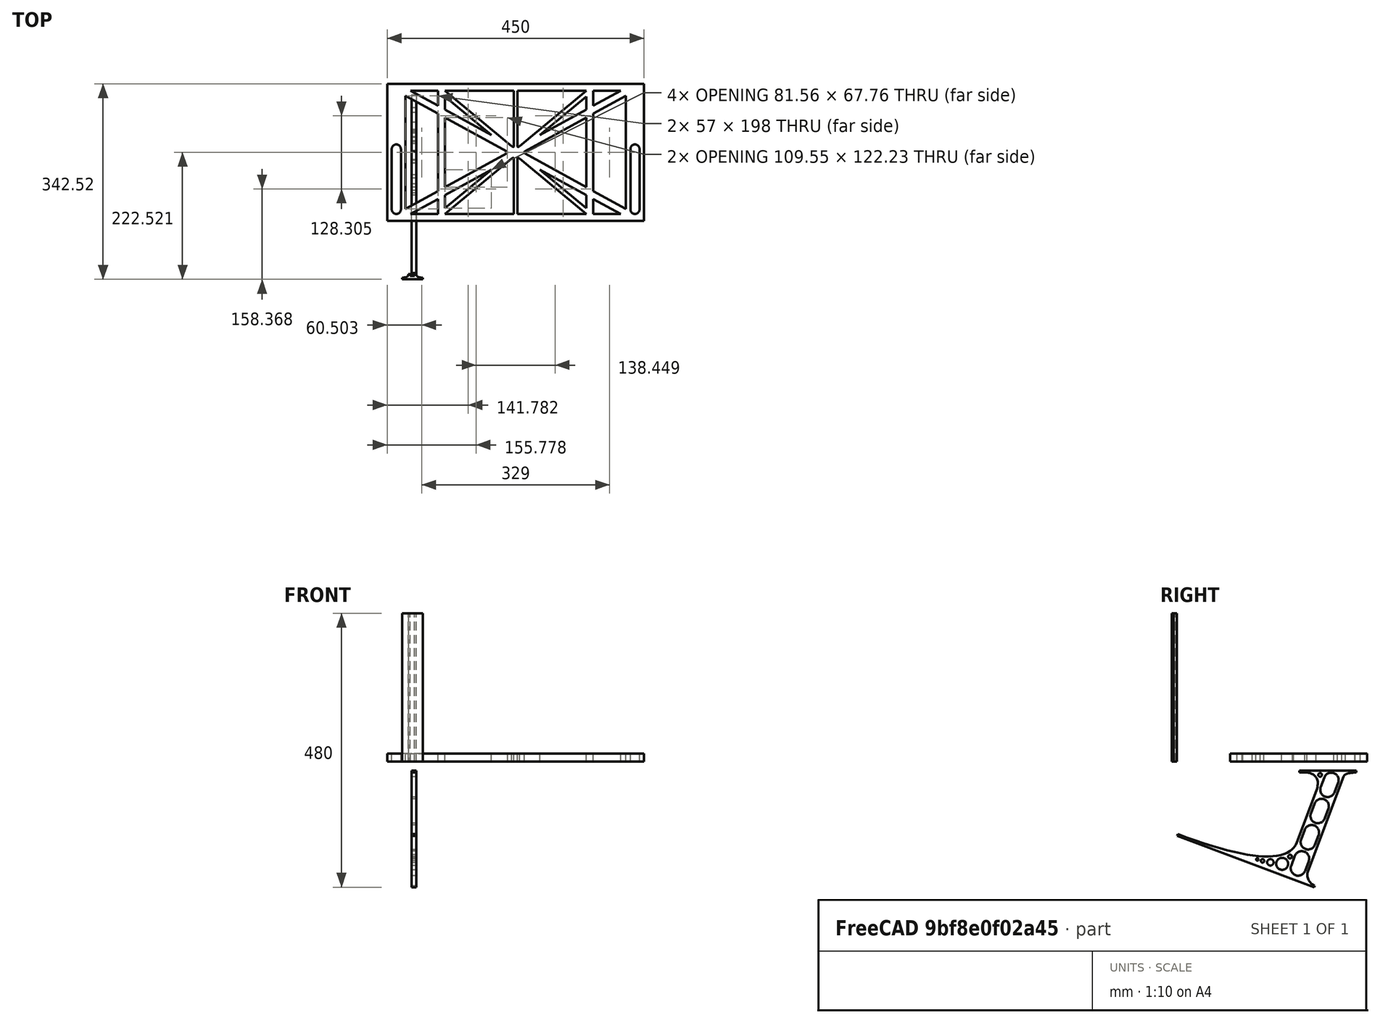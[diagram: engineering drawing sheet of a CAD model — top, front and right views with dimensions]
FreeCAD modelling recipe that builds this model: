
FCSTD DOCUMENT  (FreeCAD 0.19R0.19.2)
Label: laptopStand060
License: All rights reserved
LicenseURL: http://en.wikipedia.org/wiki/All_rights_reserved
objects: Sketcher::SketchObject×3, Part::Extrusion×3
note: 6 computed .brp shape members not serialized (recipe doc carries the construction recipe); baked Part::Feature solids carry a one-line shape summary decoded from their .brp

FEATURE [Sketcher::SketchObject] Sketch
  FullyConstrained = false
  sketch-geometry (102):
    g0: LineSegment StartX=375.073 StartY=115.221 StartZ=0 EndX=318.073 EndY=83.9235 EndZ=0
    g1: LineSegment StartX=-10.9272 StartY=-82.7794 StartZ=0 EndX=46.0728 EndY=-51.4823 EndZ=0
    g2: LineSegment StartX=-1.92719 StartY=124.221 StartZ=0 EndX=46.0728 EndY=97.8651 EndZ=0
    g3: LineSegment StartX=366.073 StartY=-91.7794 StartZ=0 EndX=318.073 EndY=-65.424 EndZ=0
    g4: LineSegment StartX=-10.9272 StartY=115.221 StartZ=0 EndX=-10.9272 EndY=-82.7794 EndZ=0
    g5: LineSegment StartX=375.073 StartY=-82.7794 StartZ=0 EndX=375.073 EndY=115.221 EndZ=0
    g6: LineSegment StartX=-1.92719 StartY=-91.7794 StartZ=0 EndX=46.0728 EndY=-91.7794 EndZ=0
    g7: LineSegment StartX=318.073 StartY=124.221 StartZ=0 EndX=366.073 EndY=124.221 EndZ=0
    g8: LineSegment StartX=306.073 StartY=-81.8102 StartZ=0 EndX=224.513 EndY=-14.0532 EndZ=0
    g9: LineSegment StartX=58.0728 StartY=114.251 StartZ=0 EndX=139.632 EndY=46.4944 EndZ=0
    g10: LineSegment StartX=306.073 StartY=124.221 StartZ=0 EndX=189.124 EndY=27.0628 EndZ=0
    g11: LineSegment StartX=58.0728 StartY=-91.7794 StartZ=0 EndX=175.022 EndY=5.37834 EndZ=0
    g12: LineSegment StartX=46.0728 StartY=124.221 StartZ=0 EndX=46.0728 EndY=97.8651 EndZ=0
    g13: LineSegment StartX=58.0728 StartY=-81.8102 StartZ=0 EndX=58.0728 EndY=-58.8351 EndZ=0
    g14: LineSegment StartX=318.073 StartY=124.221 StartZ=0 EndX=318.073 EndY=97.8651 EndZ=0
    g15: LineSegment StartX=306.073 StartY=114.251 StartZ=0 EndX=306.073 EndY=91.2763 EndZ=0
    g16: LineSegment StartX=224.513 StartY=46.4944 StartZ=0 EndX=306.073 EndY=114.251 EndZ=0
    g17: LineSegment StartX=175.022 StartY=27.0628 StartZ=0 EndX=58.0728 EndY=124.221 EndZ=0
    g18: LineSegment StartX=139.632 StartY=-14.0532 StartZ=0 EndX=58.0728 EndY=-81.8102 EndZ=0
    g19: LineSegment StartX=224.513 StartY=46.4944 StartZ=0 EndX=306.073 EndY=91.2763 EndZ=0
    g20: LineSegment StartX=139.632 StartY=-14.0532 StartZ=0 EndX=58.0728 EndY=-58.8351 EndZ=0
    g21: LineSegment StartX=189.124 StartY=5.37834 StartZ=0 EndX=306.073 EndY=-91.7794 EndZ=0
    g22: LineSegment StartX=306.073 StartY=77.3346 StartZ=0 EndX=306.073 EndY=-44.8935 EndZ=0
    g23: LineSegment StartX=318.073 StartY=83.9235 StartZ=0 EndX=318.073 EndY=-51.4823 EndZ=0
    g24: LineSegment StartX=318.073 StartY=97.8651 StartZ=0 EndX=366.073 EndY=124.221 EndZ=0
    g25: LineSegment StartX=306.073 StartY=-58.8351 StartZ=0 EndX=224.513 EndY=-14.0532 EndZ=0
    g26: LineSegment StartX=306.073 StartY=-58.8351 StartZ=0 EndX=306.073 EndY=-81.8102 EndZ=0
    g27: LineSegment StartX=318.073 StartY=-51.4823 StartZ=0 EndX=375.073 EndY=-82.7794 EndZ=0
    g28: LineSegment StartX=318.073 StartY=-65.424 StartZ=0 EndX=318.073 EndY=-91.7794 EndZ=0
    g29: LineSegment StartX=318.073 StartY=-91.7794 StartZ=0 EndX=366.073 EndY=-91.7794 EndZ=0
    g30: LineSegment StartX=58.0728 StartY=-44.8935 StartZ=0 EndX=58.0728 EndY=77.3346 EndZ=0
    g31: LineSegment StartX=46.0728 StartY=-65.424 StartZ=0 EndX=-1.92719 EndY=-91.7794 EndZ=0
    g32: LineSegment StartX=46.0728 StartY=-65.424 StartZ=0 EndX=46.0728 EndY=-91.7794 EndZ=0
    g33: LineSegment StartX=58.0728 StartY=91.2763 StartZ=0 EndX=58.0728 EndY=114.251 EndZ=0
    g34: LineSegment StartX=46.0728 StartY=77.3346 StartZ=0 EndX=46.0728 EndY=-51.4823 EndZ=0
    g35: LineSegment StartX=46.0728 StartY=124.221 StartZ=0 EndX=-1.92719 EndY=124.221 EndZ=0
    g36: LineSegment StartX=58.0728 StartY=91.2763 StartZ=0 EndX=139.632 EndY=46.4944 EndZ=0
    g37: LineSegment StartX=46.0728 StartY=83.9235 StartZ=0 EndX=-10.9272 EndY=115.221 EndZ=0
    g38: LineSegment StartX=-42.9272 StartY=136.221 StartZ=0 EndX=-42.9272 EndY=-103.779 EndZ=0
    g39: LineSegment StartX=407.073 StartY=136.221 StartZ=0 EndX=407.073 EndY=-103.779 EndZ=0
    g40: LineSegment StartX=179.022 StartY=27.0628 StartZ=0 EndX=179.022 EndY=124.221 EndZ=0
    g41: LineSegment StartX=185.124 StartY=27.0628 StartZ=0 EndX=185.124 EndY=124.221 EndZ=0
    g42: ArcOfCircle CenterX=-26.9272 CenterY=22.1087 CenterZ=0 NormalX=0 NormalY=0 NormalZ=1 AngleXU=0 Radius=8 StartAngle=1e-16 EndAngle=3.14159
    g43: ArcOfCircle CenterX=-26.9272 CenterY=-83.7794 CenterZ=0 NormalX=0 NormalY=0 NormalZ=1 AngleXU=0 Radius=8 StartAngle=3.14159 EndAngle=6.28319
    g44: LineSegment StartX=-34.9272 StartY=22.1087 StartZ=0 EndX=-34.9272 EndY=-83.7794 EndZ=0
    g45: LineSegment StartX=-18.9272 StartY=22.1087 StartZ=0 EndX=-18.9272 EndY=-83.7794 EndZ=0
    g46: LineSegment StartX=185.124 StartY=-91.7794 StartZ=0 EndX=306.073 EndY=-91.7794 EndZ=0
    g47: LineSegment StartX=179.022 StartY=-91.7794 StartZ=0 EndX=58.0728 EndY=-91.7794 EndZ=0
    g48: LineSegment StartX=306.073 StartY=124.221 StartZ=0 EndX=185.124 EndY=124.221 EndZ=0
    g49: LineSegment StartX=179.022 StartY=124.221 StartZ=0 EndX=58.0728 EndY=124.221 EndZ=0
    g50: ArcOfCircle CenterX=391.073 CenterY=22.1087 CenterZ=0 NormalX=0 NormalY=0 NormalZ=1 AngleXU=0 Radius=8 StartAngle=-4.4e-15 EndAngle=3.14159
    g51: LineSegment StartX=399.073 StartY=22.1087 StartZ=0 EndX=399.073 EndY=-83.7794 EndZ=0
    g52: LineSegment StartX=383.073 StartY=22.1087 StartZ=0 EndX=383.073 EndY=-83.7794 EndZ=0
    g53: ArcOfCircle CenterX=391.073 CenterY=-83.7794 CenterZ=0 NormalX=0 NormalY=0 NormalZ=1 AngleXU=0 Radius=8 StartAngle=3.14159 EndAngle=6.28319
    g54: Circle CenterX=175.022 CenterY=27.0628 CenterZ=0 NormalX=0 NormalY=0 NormalZ=1 AngleXU=0 Radius=1
    g55: Circle CenterX=179.022 CenterY=24.8665 CenterZ=0 NormalX=0 NormalY=0 NormalZ=1 AngleXU=0 Radius=1
    g56: Circle CenterX=179.022 CenterY=27.0628 CenterZ=0 NormalX=0 NormalY=0 NormalZ=1 AngleXU=0 Radius=1
    g57: BSplineCurve PolesCount=3 KnotsCount=2 Degree=2 IsPeriodic=0
    g58: GeomPoint X=175.022 Y=27.0628 Z=0
    g59: GeomPoint X=179.022 Y=27.0628 Z=0
    g60: Circle CenterX=189.124 CenterY=27.0628 CenterZ=0 NormalX=0 NormalY=0 NormalZ=1 AngleXU=0 Radius=1
    g61: Circle CenterX=185.124 CenterY=24.8665 CenterZ=0 NormalX=0 NormalY=0 NormalZ=1 AngleXU=0 Radius=1
    g62: Circle CenterX=185.124 CenterY=27.0628 CenterZ=0 NormalX=0 NormalY=0 NormalZ=1 AngleXU=0 Radius=1
    g63: BSplineCurve PolesCount=3 KnotsCount=2 Degree=2 IsPeriodic=0
    g64: GeomPoint X=189.124 Y=27.0628 Z=0
    g65: GeomPoint X=185.124 Y=27.0628 Z=0
    g66: Circle CenterX=175.022 CenterY=5.37834 CenterZ=0 NormalX=0 NormalY=0 NormalZ=1 AngleXU=0 Radius=1
    g67: Circle CenterX=179.022 CenterY=7.57463 CenterZ=0 NormalX=0 NormalY=0 NormalZ=1 AngleXU=0 Radius=1
    g68: Circle CenterX=179.022 CenterY=5.34704 CenterZ=0 NormalX=0 NormalY=0 NormalZ=1 AngleXU=0 Radius=1
    g69: BSplineCurve PolesCount=3 KnotsCount=2 Degree=2 IsPeriodic=0
    g70: GeomPoint X=175.022 Y=5.37834 Z=0
    g71: GeomPoint X=179.022 Y=5.34704 Z=0
    g72: Circle CenterX=189.124 CenterY=5.37834 CenterZ=0 NormalX=0 NormalY=0 NormalZ=1 AngleXU=0 Radius=1
    g73: Circle CenterX=185.124 CenterY=7.57463 CenterZ=0 NormalX=0 NormalY=0 NormalZ=1 AngleXU=0 Radius=1
    g74: Circle CenterX=185.124 CenterY=5.34704 CenterZ=0 NormalX=0 NormalY=0 NormalZ=1 AngleXU=0 Radius=1
    g75: BSplineCurve PolesCount=3 KnotsCount=2 Degree=2 IsPeriodic=0
    g76: GeomPoint X=189.124 Y=5.37834 Z=0
    g77: GeomPoint X=185.124 Y=5.34704 Z=0
    g78: LineSegment StartX=179.022 StartY=5.34704 StartZ=0 EndX=179.022 EndY=-91.7794 EndZ=0
    g79: LineSegment StartX=185.124 StartY=-91.7794 StartZ=0 EndX=185.124 EndY=5.34704 EndZ=0
    g80: Circle CenterX=165.871 CenterY=18.1458 CenterZ=0 NormalX=0 NormalY=0 NormalZ=1 AngleXU=0 Radius=1
    g81: Circle CenterX=169.377 CenterY=16.2206 CenterZ=0 NormalX=0 NormalY=0 NormalZ=1 AngleXU=0 Radius=1
    g82: Circle CenterX=165.871 CenterY=14.2954 CenterZ=0 NormalX=0 NormalY=0 NormalZ=1 AngleXU=0 Radius=1
    g83: BSplineCurve PolesCount=3 KnotsCount=2 Degree=2 IsPeriodic=0
    g84: GeomPoint X=165.871 Y=18.1458 Z=0
    g85: GeomPoint X=165.871 Y=14.2954 Z=0
    g86: Circle CenterX=198.275 CenterY=18.1458 CenterZ=0 NormalX=0 NormalY=0 NormalZ=1 AngleXU=0 Radius=1
    g87: Circle CenterX=194.768 CenterY=16.2206 CenterZ=0 NormalX=0 NormalY=0 NormalZ=1 AngleXU=0 Radius=1
    g88: Circle CenterX=198.275 CenterY=14.2954 CenterZ=0 NormalX=0 NormalY=0 NormalZ=1 AngleXU=0 Radius=1
    g89: BSplineCurve PolesCount=3 KnotsCount=2 Degree=2 IsPeriodic=0
    g90: GeomPoint X=198.275 Y=18.1458 Z=0
    g91: GeomPoint X=198.275 Y=14.2954 Z=0
    g92: LineSegment StartX=165.871 StartY=18.1458 StartZ=0 EndX=58.0728 EndY=77.3346 EndZ=0
    g93: LineSegment StartX=58.0728 StartY=-44.8935 StartZ=0 EndX=165.871 EndY=14.2954 EndZ=0
    g94: LineSegment StartX=198.275 StartY=18.1458 StartZ=0 EndX=306.073 EndY=77.3346 EndZ=0
    g95: LineSegment StartX=198.275 StartY=14.2954 StartZ=0 EndX=306.073 EndY=-44.8935 EndZ=0
    g96: LineSegment StartX=407.073 StartY=-103.779 StartZ=0 EndX=-42.9272 EndY=-103.779 EndZ=0
    g97: LineSegment StartX=407.073 StartY=136.221 StartZ=0 EndX=-42.9272 EndY=136.221 EndZ=0
    g98: LineSegment StartX=-26.9272 StartY=136.221 StartZ=0 EndX=-26.9272 EndY=98.2206 EndZ=0
    g99: LineSegment StartX=46.0728 StartY=77.3346 StartZ=0 EndX=-10.9272 EndY=77.3346 EndZ=0
    g100: LineSegment StartX=46.0728 StartY=97.8651 StartZ=0 EndX=46.0728 EndY=105.865 EndZ=0
    g101: LineSegment StartX=46.0728 StartY=105.865 StartZ=0 EndX=-10.9272 EndY=105.865 EndZ=0
  constraints (187):
    c: Horizontal(g6)
    c: Horizontal(g7)
    c: Coincident(g36,g9)
    c: Coincident(g16,g19)
    c: Coincident(g20,g18)
    c: Coincident(g25,g8)
    c: Coincident(g16,g15)
    c: Tangent(g15,g22)
    c: Tangent(g14,g23)
    c: Coincident(g19,g15)
    c: Tangent(g19,g24)
    c: Coincident(g0,g23)
    c: Coincident(g26,g8)
    c: Tangent(g3,g25)
    c: Tangent(g22,g26)
    c: Coincident(g23,g27)
    c: Coincident(g28,g3)
    c: Tangent(g23,g28)
    c: Coincident(g18,g13)
    c: Tangent(g13,g30)
    c: Coincident(g20,g13)
    c: Tangent(g20,g31)
    c: Coincident(g32,g31)
    c: Tangent(g12,g32)
    c: Coincident(g1,g34)
    c: Tangent(g30,g33)
    c: Tangent(g12,g34)
    c: Coincident(g9,g33)
    c: Coincident(g2,g12)
    c: Coincident(g36,g33)
    c: Tangent(g2,g36)
    c: Block(g17)
    c: Block(g10)
    c: Block(g14)
    c: Block(g24)
    c: Block(g0)
    c: Block(g27)
    c: Block(g5)
    c: Block(g25)
    c: Block(g26)
    c: Block(g3)
    c: Block(g28)
    c: Block(g16)
    c: Block(g21)
    c: Block(g11)
    c: Block(g20)
    c: Block(g18)
    c: Block(g32)
    c: Block(g31)
    c: Block(g1)
    c: Block(g4)
    c: Block(g37)
    c: Block(g2)
    c: Block(g12)
    c: Block(g9)
    c: Block(g33)
    c: Block(g22)
    c: Block(g35)
    c: Block(g7)
    c: Block(g29)
    c: Block(g6)
    c: Vertical(g38)
    c: Vertical(g39)
    c: Block(g39)
    c: Block(g38)
    c: Vertical(g40)
    c: Vertical(g41)
    c: Block(g40)
    c: Block(g41)
    c: Tangent(g42,g45) = 1.5708
    c: Tangent(g42,g44) = -1.5708
    c: Tangent(g44,g43) = -1.5708
    c: Tangent(g45,g43) = 1.5708
    c: Vertical(g44)
    c: Equal(g42,g43)
    c: Block(g45)
    c: Block(g44)
    c: Coincident(g46,g21)
    c: Horizontal(g46)
    c: Coincident(g47,g11)
    c: Horizontal(g47)
    c: Coincident(g48,g10)
    c: Coincident(g48,g41)
    c: Horizontal(g48)
    c: Coincident(g49,g40)
    c: Coincident(g49,g17)
    c: Horizontal(g49)
    c: Tangent(g50,g51) = 1.5708
    c: Tangent(g51,g53) = 1.5708
    c: Equal(g50,g53)
    c: Coincident(g52,g50)
    c: Coincident(g52,g53)
    c: Block(g51)
    c: Block(g52)
    c: Coincident(g57,g17)
    c: Weight(g54) = 1
    c: Equal(g54,g55)
    c: Equal(g54,g56)
    c: Coincident(g57,g40)
    c: InternalAlignment(g54,g57)
    c: InternalAlignment(g55,g57)
    c: InternalAlignment(g56,g57)
    c: InternalAlignment(g58,g57)
    c: InternalAlignment(g59,g57)
    c: Coincident(g63,g10)
    c: Weight(g60) = 1
    c: Equal(g60,g61)
    c: Equal(g60,g62)
    c: Coincident(g63,g41)
    c: InternalAlignment(g60,g63)
    c: InternalAlignment(g61,g63)
    c: InternalAlignment(g62,g63)
    c: InternalAlignment(g64,g63)
    c: InternalAlignment(g65,g63)
    c: Block(g63)
    c: Block(g57)
    c: Coincident(g69,g11)
    c: Weight(g66) = 1
    c: Equal(g66,g67)
    c: Equal(g66,g68)
    c: InternalAlignment(g66,g69)
    c: InternalAlignment(g67,g69)
    c: InternalAlignment(g68,g69)
    c: InternalAlignment(g70,g69)
    c: InternalAlignment(g71,g69)
    c: Weight(g72) = 1
    c: Equal(g72,g73)
    c: Equal(g72,g74)
    c: InternalAlignment(g72,g75)
    c: InternalAlignment(g73,g75)
    c: InternalAlignment(g74,g75)
    c: InternalAlignment(g76,g75)
    c: InternalAlignment(g77,g75)
    c: Block(g75)
    c: Block(g69)
    c: Coincident(g78,g69)
    c: Coincident(g78,g47)
    c: Vertical(g78)
    c: Coincident(g79,g46)
    c: Coincident(g79,g75)
    c: Vertical(g79)
    c: Weight(g80) = 1
    c: Equal(g80,g81)
    c: Equal(g80,g82)
    c: InternalAlignment(g80,g83)
    c: InternalAlignment(g81,g83)
    c: InternalAlignment(g82,g83)
    c: InternalAlignment(g84,g83)
    c: InternalAlignment(g85,g83)
    c: Weight(g86) = 1
    c: Equal(g86,g87)
    c: Equal(g86,g88)
    c: InternalAlignment(g86,g89)
    c: InternalAlignment(g87,g89)
    c: InternalAlignment(g88,g89)
    c: InternalAlignment(g90,g89)
    c: InternalAlignment(g91,g89)
    c: Block(g83)
    c: Block(g89)
    c: Coincident(g92,g83)
    c: Coincident(g92,g30)
    c: Coincident(g93,g30)
    c: Coincident(g93,g83)
    c: Coincident(g94,g89)
    c: Coincident(g94,g22)
    c: Coincident(g95,g89)
    c: Coincident(g95,g22)
    c: Block(g30)
    c: Coincident(g96,g39)
    c: Coincident(g96,g38)
    c: Horizontal(g96)
    c: Distance(g96) = 450
    c: Coincident(g97,g39)
    c: Coincident(g97,g38)
    c: Horizontal(g97)
    c: PointOnObject(g98,g97)
    c: Vertical(g98)
    c: Distance(g98) = 38
    c: Horizontal(g99)
    c: PointOnObject(g99,g4)
    c: Coincident(g34,g99)
    c: Coincident(g100,g2)
    c: Distance(g100) = 8
    c: Parallel(g12,g100)
    c: Coincident(g101,g100)
    c: Horizontal(g101)
    c: PointOnObject(g101,g4)
FEATURE [Sketcher::SketchObject] Sketch001
  FullyConstrained = true
  MapMode = 4
  Placement = pos=(0,0,0) rot=(0.57735,0.57735,0.57735;2.0944rad)
  Support = -> [Sketch]
  sketch-geometry (46):
    g0: BSplineCurve PolesCount=3 KnotsCount=2 Degree=2 IsPeriodic=0
    g1: ArcOfCircle CenterX=73.1223 CenterY=-32.291 CenterZ=0 NormalX=0 NormalY=0 NormalZ=1 AngleXU=0 Radius=13 StartAngle=5.92268 EndAngle=9.06428
    g2: ArcOfCircle CenterX=66.7816 CenterY=-49.1439 CenterZ=0 NormalX=0 NormalY=0 NormalZ=1 AngleXU=0 Radius=13 StartAngle=2.78068 EndAngle=5.92131
    g3: ArcOfCircle CenterX=55.9263 CenterY=-78.1807 CenterZ=0 NormalX=0 NormalY=0 NormalZ=1 AngleXU=0 Radius=13 StartAngle=5.92268 EndAngle=9.06428
    g4: ArcOfCircle CenterX=49.5884 CenterY=-95.0342 CenterZ=0 NormalX=0 NormalY=0 NormalZ=1 AngleXU=0 Radius=13 StartAngle=2.78068 EndAngle=5.92131
    g5: ArcOfCircle CenterX=38.7206 CenterY=-124.067 CenterZ=0 NormalX=0 NormalY=0 NormalZ=1 AngleXU=0 Radius=13 StartAngle=5.92268 EndAngle=9.06428
    g6: ArcOfCircle CenterX=32.3875 CenterY=-140.92 CenterZ=0 NormalX=0 NormalY=0 NormalZ=1 AngleXU=0 Radius=13 StartAngle=2.78068 EndAngle=5.92131
    g7: ArcOfCircle CenterX=21.4715 CenterY=-169.934 CenterZ=0 NormalX=0 NormalY=0 NormalZ=1 AngleXU=0 Radius=13 StartAngle=5.92268 EndAngle=9.06428
    g8: ArcOfCircle CenterX=15.1336 CenterY=-186.787 CenterZ=0 NormalX=0 NormalY=0 NormalZ=1 AngleXU=0 Radius=13 StartAngle=2.78068 EndAngle=5.92131
    g9-g12: Circle x4 (B-spline internal-alignment scaffolding for g13; pole/knot coordinates omitted)
    g13: BSplineCurve PolesCount=4 KnotsCount=2 Degree=3 IsPeriodic=0
    g14: GeomPoint X=28.8094 Y=-19.0875 Z=0
    g15: GeomPoint X=47.0443 Y=-50.4712 Z=0
    g16: Circle CenterX=53.5586 CenterY=-23.2695 CenterZ=0 NormalX=0 NormalY=0 NormalZ=1 AngleXU=0 Radius=3.24518
    g17: Circle CenterX=-195.441 CenterY=-127.082 CenterZ=0 NormalX=0 NormalY=0 NormalZ=1 AngleXU=0 Radius=1
    g18: Circle CenterX=-8.24091 CenterY=-197.481 CenterZ=0 NormalX=0 NormalY=0 NormalZ=1 AngleXU=0 Radius=1
    g19: Circle CenterX=12.8789 CenterY=-141.321 CenterZ=0 NormalX=0 NormalY=0 NormalZ=1 AngleXU=0 Radius=1
    g20: BSplineCurve PolesCount=3 KnotsCount=2 Degree=2 IsPeriodic=0
    g21: GeomPoint X=-195.441 Y=-127.082 Z=0
    g22: GeomPoint X=12.8789 Y=-141.321 Z=0
    g23: Circle CenterX=-12.8016 CenterY=-179.036 CenterZ=0 NormalX=0 NormalY=0 NormalZ=1 AngleXU=0 Radius=10.5072
    g24: Circle CenterX=0.933922 CenterY=-166.43 CenterZ=0 NormalX=0 NormalY=0 NormalZ=1 AngleXU=0 Radius=3.26661
    g25: Circle CenterX=-33.5518 CenterY=-176.44 CenterZ=0 NormalX=0 NormalY=0 NormalZ=1 AngleXU=0 Radius=5.64388
    g26: Circle CenterX=-47.2366 CenterY=-173.859 CenterZ=0 NormalX=0 NormalY=0 NormalZ=1 AngleXU=0 Radius=3.01653
    g27: Circle CenterX=-56.2595 CenterY=-171.456 CenterZ=0 NormalX=0 NormalY=0 NormalZ=1 AngleXU=0 Radius=2.12826
    g28: ArcOfCircle CenterX=51.2151 CenterY=-198.473 CenterZ=0 NormalX=0 NormalY=0 NormalZ=1 AngleXU=0 Radius=20 StartAngle=2.78189 EndAngle=4.35269
    g29: LineSegment StartX=32.4951 StartY=-191.433 StartZ=0 EndX=94.6578 EndY=-26.1352 EndZ=0
    g30: LineSegment StartX=43.1192 StartY=-220.001 StartZ=0 EndX=-196.497 EndY=-129.89 EndZ=0
    g31: LineSegment StartX=43.1192 StartY=-220.001 StartZ=0 EndX=44.1752 EndY=-217.193 EndZ=0
    g32: LineSegment StartX=117.223 StartY=-19.0875 StartZ=0 EndX=117.223 EndY=-16.0875 EndZ=0
    g33: LineSegment StartX=117.223 StartY=-16.0875 StartZ=0 EndX=17.2232 EndY=-16.0875 EndZ=0
    g34: LineSegment StartX=17.2232 StartY=-16.0875 StartZ=0 EndX=17.2232 EndY=-19.0875 EndZ=0
    g35: LineSegment StartX=28.8094 StartY=-19.0875 StartZ=0 EndX=17.2232 EndY=-19.0875 EndZ=0
    g36: LineSegment StartX=47.0443 StartY=-50.4712 StartZ=0 EndX=12.8789 EndY=-141.321 EndZ=0
    g37: LineSegment StartX=-195.441 StartY=-127.082 StartZ=0 EndX=-196.497 EndY=-129.89 EndZ=0
    g38: LineSegment StartX=85.2866 StartY=-36.8766 StartZ=0 EndX=78.9396 EndY=-53.7463 EndZ=0
    g39: LineSegment StartX=60.9579 StartY=-27.7053 StartZ=0 EndX=54.6191 EndY=-44.5532 EndZ=0
    g40: LineSegment StartX=68.0907 StartY=-82.7664 StartZ=0 EndX=61.7465 EndY=-99.6365 EndZ=0
    g41: LineSegment StartX=43.7619 StartY=-73.595 StartZ=0 EndX=37.426 EndY=-90.4435 EndZ=0
    g42: LineSegment StartX=50.885 StartY=-128.652 StartZ=0 EndX=44.5456 EndY=-145.522 EndZ=0
    g43: LineSegment StartX=26.5562 StartY=-119.481 StartZ=0 EndX=20.2251 EndY=-136.329 EndZ=0
    g44: LineSegment StartX=9.3071 StartY=-165.349 StartZ=0 EndX=2.97115 EndY=-182.197 EndZ=0
    g45: LineSegment StartX=33.6358 StartY=-174.52 StartZ=0 EndX=27.2917 EndY=-191.39 EndZ=0
  constraints (71):
    c: Block(g0)
    c: Block(g1)
    c: Block(g2)
    c: Block(g4)
    c: Block(g3)
    c: Block(g6)
    c: Block(g5)
    c: Block(g8)
    c: Block(g7)
    c: Weight(g9) = 1
    c: Equal(g9,g10)
    c: Equal(g9,g11)
    c: Equal(g9,g12)
    c: InternalAlignment(g9-g12 -> g13) x4
    c: InternalAlignment(g14,g13)
    c: InternalAlignment(g15,g13)
    c: Block(g16)
    c: Weight(g17) = 1
    c: Equal(g17,g18)
    c: Equal(g17,g19)
    c: InternalAlignment(g17,g20)
    c: InternalAlignment(g18,g20)
    c: InternalAlignment(g19,g20)
    c: InternalAlignment(g21,g20)
    c: InternalAlignment(g22,g20)
    c: Block(g20)
    c: Block(g23)
    c: Block(g24)
    c: Block(g25)
    c: Block(g26)
    c: Block(g27)
    c: Block(g28)
    c: Coincident(g29,g28)
    c: Coincident(g29,g0)
    c: Block(g13)
    c: Coincident(g31,g30)
    c: Coincident(g31,g28)
    c: Block(g31)
    c: Coincident(g32,g0)
    c: Vertical(g32)
    c: Coincident(g33,g32)
    c: Horizontal(g33)
    c: Coincident(g34,g33)
    c: Vertical(g34)
    c: Block(g33)
    c: Coincident(g35,g13)
    c: Coincident(g35,g34)
    c: Horizontal(g35)
    c: Coincident(g36,g13)
    c: Coincident(g36,g20)
    c: Coincident(g37,g20)
    c: Coincident(g37,g30)
    c: Block(g30)
    c: Coincident(g38,g1)
    c: Coincident(g38,g2)
    c: Coincident(g39,g1)
    c: Coincident(g39,g2)
    c: Coincident(g40,g3)
    c: Coincident(g40,g4)
    c: Coincident(g41,g3)
    c: Coincident(g41,g4)
    c: Coincident(g42,g5)
    c: Coincident(g42,g6)
    c: Coincident(g43,g5)
    c: Coincident(g43,g6)
    c: Coincident(g44,g7)
    c: Coincident(g44,g8)
    c: Coincident(g45,g7)
    c: Coincident(g45,g8)
    c: Distance(g30) = 256
    c: Distance(g33) = 100
FEATURE [Part::Extrusion] Extrude002
  Base = -> Sketch001
  Dir = (1,0,0)
  DirMode = 2
  FaceMakerClass = Part::FaceMakerBullseye
  LengthFwd = 8
  LengthRev = 0
  Solid = true
  Symmetric = false
FEATURE [Sketcher::SketchObject] Sketch002
  FullyConstrained = true
  sketch-geometry (20):
    g0: LineSegment StartX=-2.77179 StartY=-200.304 StartZ=0 EndX=5.22821 EndY=-200.304 EndZ=0
    g1: LineSegment StartX=5.22821 StartY=-200.304 StartZ=0 EndX=5.22821 EndY=-197.304 EndZ=0
    g2: LineSegment StartX=-2.77179 StartY=-200.304 StartZ=0 EndX=-2.77179 EndY=-197.304 EndZ=0
    g3: LineSegment StartX=5.22821 StartY=-197.304 StartZ=0 EndX=8.22821 EndY=-197.304 EndZ=0
    g4: LineSegment StartX=-2.77179 StartY=-197.304 StartZ=0 EndX=-5.77179 EndY=-197.304 EndZ=0
    g5: LineSegment StartX=19.2282 StartY=-203.304 StartZ=0 EndX=19.2282 EndY=-206.304 EndZ=0
    g6: LineSegment StartX=-16.7718 StartY=-203.304 StartZ=0 EndX=-16.7718 EndY=-206.304 EndZ=0
    g7: LineSegment StartX=-16.7718 StartY=-206.304 StartZ=0 EndX=19.2282 EndY=-206.304 EndZ=0
    g8: Circle CenterX=-16.7718 CenterY=-203.304 CenterZ=0 NormalX=0 NormalY=0 NormalZ=1 AngleXU=0 Radius=1
    g9: Circle CenterX=-5.77179 CenterY=-203.304 CenterZ=0 NormalX=0 NormalY=0 NormalZ=1 AngleXU=0 Radius=1
    g10: Circle CenterX=-5.77179 CenterY=-197.304 CenterZ=0 NormalX=0 NormalY=0 NormalZ=1 AngleXU=0 Radius=1
    g11: BSplineCurve PolesCount=3 KnotsCount=2 Degree=2 IsPeriodic=0
    g12: GeomPoint X=-16.7718 Y=-203.304 Z=0
    g13: GeomPoint X=-5.77179 Y=-197.304 Z=0
    g14: Circle CenterX=19.2282 CenterY=-203.304 CenterZ=0 NormalX=0 NormalY=0 NormalZ=1 AngleXU=0 Radius=1
    g15: Circle CenterX=8.22821 CenterY=-203.304 CenterZ=0 NormalX=0 NormalY=0 NormalZ=1 AngleXU=0 Radius=1
    g16: Circle CenterX=8.22821 CenterY=-197.304 CenterZ=0 NormalX=0 NormalY=0 NormalZ=1 AngleXU=0 Radius=1
    g17: BSplineCurve PolesCount=3 KnotsCount=2 Degree=2 IsPeriodic=0
    g18: GeomPoint X=19.2282 Y=-203.304 Z=0
    g19: GeomPoint X=8.22821 Y=-197.304 Z=0
  constraints (41):
    c: Horizontal(g0)
    c: Distance(g0) = 8
    c: Coincident(g1,g0)
    c: Vertical(g1)
    c: Distance(g1) = 3
    c: Coincident(g2,g0)
    c: Vertical(g2)
    c: Distance(g2) = 3
    c: Coincident(g3,g1)
    c: Horizontal(g3)
    c: Distance(g3) = 3
    c: Coincident(g4,g2)
    c: Horizontal(g4)
    c: Distance(g4) = 3
    c: Vertical(g5)
    c: Vertical(g6)
    c: Coincident(g7,g6)
    c: Coincident(g7,g5)
    c: Weight(g8) = 1
    c: Equal(g8,g9)
    c: Equal(g8,g10)
    c: Coincident(g11,g4)
    c: InternalAlignment(g8,g11)
    c: InternalAlignment(g9,g11)
    c: InternalAlignment(g10,g11)
    c: InternalAlignment(g12,g11)
    c: InternalAlignment(g13,g11)
    c: Coincident(g17,g5)
    c: Weight(g14) = 1
    c: Equal(g14,g15)
    c: Equal(g14,g16)
    c: Coincident(g17,g3)
    c: InternalAlignment(g14,g17)
    c: InternalAlignment(g15,g17)
    c: InternalAlignment(g16,g17)
    c: InternalAlignment(g18,g17)
    c: InternalAlignment(g19,g17)
    c: Block(g7)
    c: Block(g17)
    c: Block(g11)
    c: Block(g6)
FEATURE [Part::Extrusion] Extrude003
  Base = -> Sketch002
  Dir = (0,0,1)
  DirMode = 2
  FaceMakerClass = Part::FaceMakerBullseye
  LengthFwd = 260
  LengthRev = 0
  Solid = true
  Symmetric = false
FEATURE [Part::Extrusion] Extrude
  Base = -> Sketch
  Dir = (0,0,1)
  DirMode = 2
  FaceMakerClass = Part::FaceMakerBullseye
  LengthFwd = 14
  LengthRev = 0
  Solid = true
  Symmetric = false
